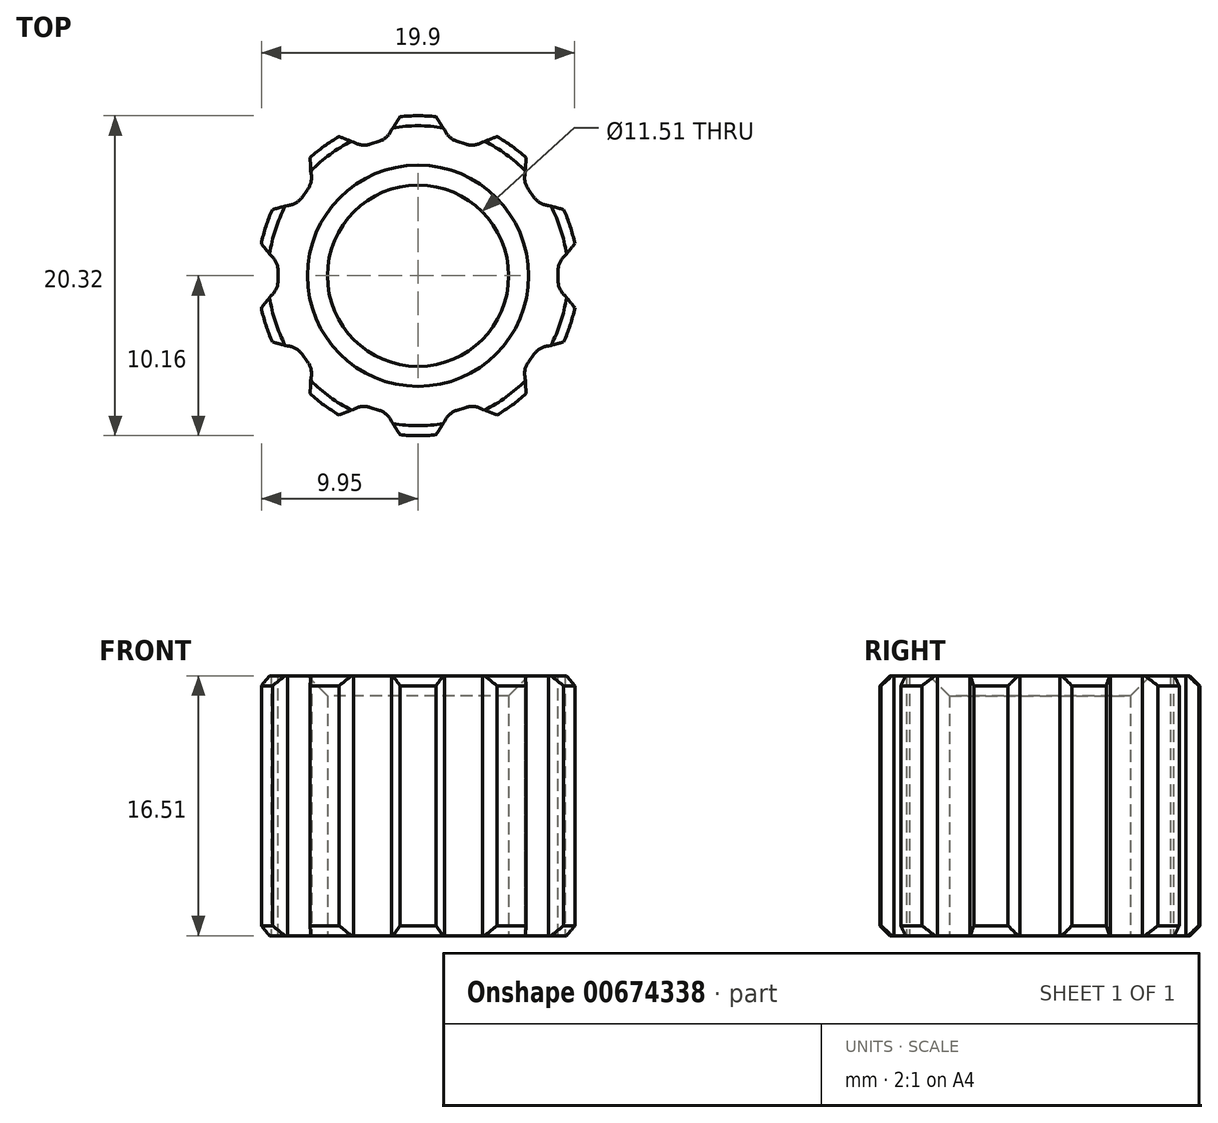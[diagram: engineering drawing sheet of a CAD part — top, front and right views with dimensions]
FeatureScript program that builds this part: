
annotation { "Feature Type Name" : "Feature", "Feature Type Description" : "" }
export const myFeature = defineFeature(function(context is Context, id is Id, definition is map)
    precondition{}
    {
        {
            var Q0;
            Q0=qCreatedBy(makeId("Top.planeOp"),FACE);
            var sketch = newSketch(context, id + "F0", { "sketchPlane" : qUnion([Q0])});
            skCircle(sketch, "E0", {"center": v(0, 0) * mm, "radius": 10.16 * mm});
            skCircle(sketch, "E1", {"center": v(0, 0) * mm, "radius": 5.75 * mm});
            skLineSegment(sketch, "E2.bottom", {"start": v(11.52, 1.27) * mm, "end": v(8.9, 1.27) * mm});
            skLineSegment(sketch, "E2.top", {"start": v(11.52, -1.27) * mm, "end": v(8.9, -1.27) * mm});
            skLineSegment(sketch, "E2.left", {"start": v(11.52, 1.27) * mm, "end": v(11.52, -1.27) * mm});
            skLineSegment(sketch, "E2.right", {"start": v(8.9, 1.27) * mm, "end": v(8.9, -1.27) * mm});
            skLineSegment(sketch, "E3.1.0", {"start": v(8.57, 7.8) * mm, "end": v(6.45, 6.25) * mm});
            skLineSegment(sketch, "E3.1.1", {"start": v(6.45, 6.25) * mm, "end": v(7.94, 4.2) * mm});
            skLineSegment(sketch, "E3.1.2", {"start": v(10.07, 5.74) * mm, "end": v(7.94, 4.2) * mm});
            skLineSegment(sketch, "E3.1.3", {"start": v(8.57, 7.8) * mm, "end": v(10.07, 5.74) * mm});
            skLineSegment(sketch, "E3.2.0", {"start": v(2.35, 11.35) * mm, "end": v(1.54, 8.85) * mm});
            skLineSegment(sketch, "E3.2.1", {"start": v(1.54, 8.85) * mm, "end": v(3.96, 8.06) * mm});
            skLineSegment(sketch, "E3.2.2", {"start": v(4.77, 10.57) * mm, "end": v(3.96, 8.06) * mm});
            skLineSegment(sketch, "E3.2.3", {"start": v(2.35, 11.35) * mm, "end": v(4.77, 10.57) * mm});
            skLineSegment(sketch, "E3.3.0", {"start": v(-4.77, 10.57) * mm, "end": v(-3.96, 8.06) * mm});
            skLineSegment(sketch, "E3.3.1", {"start": v(-3.96, 8.06) * mm, "end": v(-1.54, 8.85) * mm});
            skLineSegment(sketch, "E3.3.2", {"start": v(-2.35, 11.35) * mm, "end": v(-1.54, 8.85) * mm});
            skLineSegment(sketch, "E3.3.3", {"start": v(-4.77, 10.57) * mm, "end": v(-2.35, 11.35) * mm});
            skLineSegment(sketch, "E3.4.0", {"start": v(-10.07, 5.74) * mm, "end": v(-7.94, 4.2) * mm});
            skLineSegment(sketch, "E3.4.1", {"start": v(-7.94, 4.2) * mm, "end": v(-6.45, 6.25) * mm});
            skLineSegment(sketch, "E3.4.2", {"start": v(-8.57, 7.8) * mm, "end": v(-6.45, 6.25) * mm});
            skLineSegment(sketch, "E3.4.3", {"start": v(-10.07, 5.74) * mm, "end": v(-8.57, 7.8) * mm});
            skLineSegment(sketch, "E3.5.0", {"start": v(-11.52, -1.27) * mm, "end": v(-8.9, -1.27) * mm});
            skLineSegment(sketch, "E3.5.1", {"start": v(-8.9, -1.27) * mm, "end": v(-8.9, 1.27) * mm});
            skLineSegment(sketch, "E3.5.2", {"start": v(-11.52, 1.27) * mm, "end": v(-8.9, 1.27) * mm});
            skLineSegment(sketch, "E3.5.3", {"start": v(-11.52, -1.27) * mm, "end": v(-11.52, 1.27) * mm});
            skLineSegment(sketch, "E3.6.0", {"start": v(-8.57, -7.8) * mm, "end": v(-6.45, -6.25) * mm});
            skLineSegment(sketch, "E3.6.1", {"start": v(-6.45, -6.25) * mm, "end": v(-7.94, -4.2) * mm});
            skLineSegment(sketch, "E3.6.2", {"start": v(-10.07, -5.74) * mm, "end": v(-7.94, -4.2) * mm});
            skLineSegment(sketch, "E3.6.3", {"start": v(-8.57, -7.8) * mm, "end": v(-10.07, -5.74) * mm});
            skLineSegment(sketch, "E3.7.0", {"start": v(-2.35, -11.35) * mm, "end": v(-1.54, -8.85) * mm});
            skLineSegment(sketch, "E3.7.1", {"start": v(-1.54, -8.85) * mm, "end": v(-3.96, -8.06) * mm});
            skLineSegment(sketch, "E3.7.2", {"start": v(-4.77, -10.57) * mm, "end": v(-3.96, -8.06) * mm});
            skLineSegment(sketch, "E3.7.3", {"start": v(-2.35, -11.35) * mm, "end": v(-4.77, -10.57) * mm});
            skLineSegment(sketch, "E3.8.0", {"start": v(4.77, -10.57) * mm, "end": v(3.96, -8.06) * mm});
            skLineSegment(sketch, "E3.8.1", {"start": v(3.96, -8.06) * mm, "end": v(1.54, -8.85) * mm});
            skLineSegment(sketch, "E3.8.2", {"start": v(2.35, -11.35) * mm, "end": v(1.54, -8.85) * mm});
            skLineSegment(sketch, "E3.8.3", {"start": v(4.77, -10.57) * mm, "end": v(2.35, -11.35) * mm});
            skLineSegment(sketch, "E3.9.0", {"start": v(10.07, -5.74) * mm, "end": v(7.94, -4.2) * mm});
            skLineSegment(sketch, "E3.9.1", {"start": v(7.94, -4.2) * mm, "end": v(6.45, -6.25) * mm});
            skLineSegment(sketch, "E3.9.2", {"start": v(8.57, -7.8) * mm, "end": v(6.45, -6.25) * mm});
            skLineSegment(sketch, "E3.9.3", {"start": v(10.07, -5.74) * mm, "end": v(8.57, -7.8) * mm});
            skSolve(sketch);
        }
        {
            var Q0;
            Q0=makeQuery(id+"F0.imprint","IMPRINT",FACE,{"disambiguationData":[TD([[makeQuery(id+"F0.imprint","IMPRINT",EDGE,{"derivedFrom":sQuery(id+"F0.wireOp",EDGE,"E1")}),-1.0]])]});
            extrude(context, id + "F1", {"entities" : qUnion([Q0]), "depth" : 16.5 * mm, "offsetDistance" : 25.4 * mm});
        }
        {
            var Q0;
            Q0=makeQuery(id+"F1.opExtrude","SWEPT_EDGE",EDGE,{"disambiguationData":[OSD([sQuery(id+"F0.wireOp",EDGE,"E0"),sQuery(id+"F0.wireOp",EDGE,"E3.1.0")])]});
            var Q1;
            Q1=makeQuery(id+"F1.opExtrude","SWEPT_EDGE",EDGE,{"disambiguationData":[OSD([sQuery(id+"F0.wireOp",EDGE,"E0"),sQuery(id+"F0.wireOp",EDGE,"E3.2.2")])]});
            var Q2;
            {var subQ0=sQuery(id+"F0.wireOp",EDGE,"E0");Q2=makeQuery(id+"F1.opExtrude","SWEPT_FACE",FACE,{"disambiguationData":[OSD([subQ0]),TDD([makeQuery(id+"F0.imprint","IMPRINT",EDGE,{"disambiguationData":[TD([[makeQuery(id+"F0.imprint","INTERSECT",VERTEX,{"derivedFrom":[subQ0,sQuery(id+"F0.wireOp",EDGE,"E3.1.2")]}),1.0]])],"derivedFrom":subQ0})])]});}
            var Q3;
            {var subQ0=sQuery(id+"F0.wireOp",EDGE,"E0");Q3=makeQuery(id+"F1.opExtrude","SWEPT_FACE",FACE,{"disambiguationData":[OSD([subQ0]),TDD([makeQuery(id+"F0.imprint","IMPRINT",EDGE,{"disambiguationData":[TD([[makeQuery(id+"F0.imprint","INTERSECT",VERTEX,{"derivedFrom":[subQ0,sQuery(id+"F0.wireOp",EDGE,"E3.1.0")]}),-1.0]])],"derivedFrom":subQ0})])]});}
            var Q4;
            {var subQ0=sQuery(id+"F0.wireOp",EDGE,"E0");Q4=makeQuery(id+"F1.opExtrude","SWEPT_FACE",FACE,{"disambiguationData":[OSD([subQ0]),TDD([makeQuery(id+"F0.imprint","IMPRINT",EDGE,{"disambiguationData":[TD([[makeQuery(id+"F0.imprint","INTERSECT",VERTEX,{"derivedFrom":[subQ0,sQuery(id+"F0.wireOp",EDGE,"E3.2.0")]}),-1.0]])],"derivedFrom":subQ0})])]});}
            var Q5;
            {var subQ0=sQuery(id+"F0.wireOp",EDGE,"E0");Q5=makeQuery(id+"F1.opExtrude","SWEPT_FACE",FACE,{"disambiguationData":[OSD([subQ0]),TDD([makeQuery(id+"F0.imprint","IMPRINT",EDGE,{"disambiguationData":[TD([[makeQuery(id+"F0.imprint","INTERSECT",VERTEX,{"derivedFrom":[subQ0,sQuery(id+"F0.wireOp",EDGE,"E3.3.0")]}),-1.0]])],"derivedFrom":subQ0})])]});}
            var Q6;
            {var subQ0=sQuery(id+"F0.wireOp",EDGE,"E0");Q6=makeQuery(id+"F1.opExtrude","SWEPT_FACE",FACE,{"disambiguationData":[OSD([subQ0]),TDD([makeQuery(id+"F0.imprint","IMPRINT",EDGE,{"disambiguationData":[TD([[makeQuery(id+"F0.imprint","INTERSECT",VERTEX,{"derivedFrom":[subQ0,sQuery(id+"F0.wireOp",EDGE,"E3.4.0")]}),-1.0]])],"derivedFrom":subQ0})])]});}
            var Q7;
            {var subQ0=sQuery(id+"F0.wireOp",EDGE,"E0");Q7=makeQuery(id+"F1.opExtrude","SWEPT_FACE",FACE,{"disambiguationData":[OSD([subQ0]),TDD([makeQuery(id+"F0.imprint","IMPRINT",EDGE,{"disambiguationData":[TD([[makeQuery(id+"F0.imprint","INTERSECT",VERTEX,{"derivedFrom":[subQ0,sQuery(id+"F0.wireOp",EDGE,"E3.5.0")]}),-1.0]])],"derivedFrom":subQ0})])]});}
            var Q8;
            {var subQ0=sQuery(id+"F0.wireOp",EDGE,"E0");Q8=makeQuery(id+"F1.opExtrude","SWEPT_FACE",FACE,{"disambiguationData":[OSD([subQ0]),TDD([makeQuery(id+"F0.imprint","IMPRINT",EDGE,{"disambiguationData":[TD([[makeQuery(id+"F0.imprint","INTERSECT",VERTEX,{"derivedFrom":[subQ0,sQuery(id+"F0.wireOp",EDGE,"E3.6.0")]}),-1.0]])],"derivedFrom":subQ0})])]});}
            var Q9;
            {var subQ0=sQuery(id+"F0.wireOp",EDGE,"E0");Q9=makeQuery(id+"F1.opExtrude","SWEPT_FACE",FACE,{"disambiguationData":[OSD([subQ0]),TDD([makeQuery(id+"F0.imprint","IMPRINT",EDGE,{"disambiguationData":[TD([[makeQuery(id+"F0.imprint","INTERSECT",VERTEX,{"derivedFrom":[subQ0,sQuery(id+"F0.wireOp",EDGE,"E3.7.0")]}),-1.0]])],"derivedFrom":subQ0})])]});}
            var Q10;
            {var subQ0=sQuery(id+"F0.wireOp",EDGE,"E0");Q10=makeQuery(id+"F1.opExtrude","SWEPT_FACE",FACE,{"disambiguationData":[OSD([subQ0]),TDD([makeQuery(id+"F0.imprint","IMPRINT",EDGE,{"disambiguationData":[TD([[makeQuery(id+"F0.imprint","INTERSECT",VERTEX,{"derivedFrom":[subQ0,sQuery(id+"F0.wireOp",EDGE,"E3.8.0")]}),-1.0]])],"derivedFrom":subQ0})])]});}
            var Q11;
            {var subQ0=sQuery(id+"F0.wireOp",EDGE,"E0");Q11=makeQuery(id+"F1.opExtrude","SWEPT_FACE",FACE,{"disambiguationData":[OSD([subQ0]),TDD([makeQuery(id+"F0.imprint","IMPRINT",EDGE,{"disambiguationData":[TD([[makeQuery(id+"F0.imprint","INTERSECT",VERTEX,{"derivedFrom":[subQ0,sQuery(id+"F0.wireOp",EDGE,"E3.9.0")]}),-1.0]])],"derivedFrom":subQ0})])]});}
            chamfer(context, id + "F2", {"entities" : qUnion([Q0, Q1, Q2, Q3, Q4, Q5, Q6, Q7, Q8, Q9, Q10, Q11]), "width" : 0.64 * mm, "tangentPropagation" : true});
        }
        {
            var Q0;
            Q0=makeQuery(id+"F1.opExtrude","CAP_EDGE",EDGE,{"disambiguationData":[OSD([sQuery(id+"F0.wireOp",EDGE,"E1")])],"isStart":false});
            chamfer(context, id + "F3", {"entities" : qUnion([Q0]), "width" : 1.27 * mm, "tangentPropagation" : true});
        }
        {
            var Q0;
            Q0=makeQuery(id+"F1.opExtrude","SWEPT_EDGE",EDGE,{"disambiguationData":[OSD([sQuery(id+"F0.wireOp",EDGE,"E3.8.0"),sQuery(id+"F0.wireOp",EDGE,"E3.8.1")])]});
            var Q1;
            Q1=makeQuery(id+"F1.opExtrude","SWEPT_EDGE",EDGE,{"disambiguationData":[OSD([sQuery(id+"F0.wireOp",EDGE,"E3.8.1"),sQuery(id+"F0.wireOp",EDGE,"E3.8.2")])]});
            var Q2;
            Q2=makeQuery(id+"F1.opExtrude","SWEPT_EDGE",EDGE,{"disambiguationData":[OSD([sQuery(id+"F0.wireOp",EDGE,"E3.7.0"),sQuery(id+"F0.wireOp",EDGE,"E3.7.1")])]});
            var Q3;
            Q3=makeQuery(id+"F1.opExtrude","SWEPT_EDGE",EDGE,{"disambiguationData":[OSD([sQuery(id+"F0.wireOp",EDGE,"E3.7.1"),sQuery(id+"F0.wireOp",EDGE,"E3.7.2")])]});
            var Q4;
            Q4=makeQuery(id+"F1.opExtrude","SWEPT_EDGE",EDGE,{"disambiguationData":[OSD([sQuery(id+"F0.wireOp",EDGE,"E3.6.0"),sQuery(id+"F0.wireOp",EDGE,"E3.6.1")])]});
            var Q5;
            Q5=makeQuery(id+"F1.opExtrude","SWEPT_EDGE",EDGE,{"disambiguationData":[OSD([sQuery(id+"F0.wireOp",EDGE,"E3.5.0"),sQuery(id+"F0.wireOp",EDGE,"E3.5.1")])]});
            var Q6;
            Q6=makeQuery(id+"F1.opExtrude","SWEPT_EDGE",EDGE,{"disambiguationData":[OSD([sQuery(id+"F0.wireOp",EDGE,"E3.4.1"),sQuery(id+"F0.wireOp",EDGE,"E3.4.2")])]});
            var Q7;
            Q7=makeQuery(id+"F1.opExtrude","SWEPT_EDGE",EDGE,{"disambiguationData":[OSD([sQuery(id+"F0.wireOp",EDGE,"E3.5.1"),sQuery(id+"F0.wireOp",EDGE,"E3.5.2")])]});
            var Q8;
            Q8=makeQuery(id+"F1.opExtrude","SWEPT_EDGE",EDGE,{"disambiguationData":[OSD([sQuery(id+"F0.wireOp",EDGE,"E3.6.1"),sQuery(id+"F0.wireOp",EDGE,"E3.6.2")])]});
            var Q9;
            Q9=makeQuery(id+"F1.opExtrude","SWEPT_EDGE",EDGE,{"disambiguationData":[OSD([sQuery(id+"F0.wireOp",EDGE,"E3.4.0"),sQuery(id+"F0.wireOp",EDGE,"E3.4.1")])]});
            var Q10;
            Q10=makeQuery(id+"F1.opExtrude","SWEPT_EDGE",EDGE,{"disambiguationData":[OSD([sQuery(id+"F0.wireOp",EDGE,"E3.3.0"),sQuery(id+"F0.wireOp",EDGE,"E3.3.1")])]});
            var Q11;
            Q11=makeQuery(id+"F1.opExtrude","SWEPT_EDGE",EDGE,{"disambiguationData":[OSD([sQuery(id+"F0.wireOp",EDGE,"E3.2.0"),sQuery(id+"F0.wireOp",EDGE,"E3.2.1")])]});
            var Q12;
            Q12=makeQuery(id+"F1.opExtrude","SWEPT_EDGE",EDGE,{"disambiguationData":[OSD([sQuery(id+"F0.wireOp",EDGE,"E3.1.1"),sQuery(id+"F0.wireOp",EDGE,"E3.1.2")])]});
            var Q13;
            Q13=makeQuery(id+"F1.opExtrude","SWEPT_EDGE",EDGE,{"disambiguationData":[OSD([sQuery(id+"F0.wireOp",EDGE,"E3.3.1"),sQuery(id+"F0.wireOp",EDGE,"E3.3.2")])]});
            var Q14;
            Q14=makeQuery(id+"F1.opExtrude","SWEPT_EDGE",EDGE,{"disambiguationData":[OSD([sQuery(id+"F0.wireOp",EDGE,"E3.2.1"),sQuery(id+"F0.wireOp",EDGE,"E3.2.2")])]});
            var Q15;
            Q15=makeQuery(id+"F1.opExtrude","SWEPT_EDGE",EDGE,{"disambiguationData":[OSD([sQuery(id+"F0.wireOp",EDGE,"E3.1.0"),sQuery(id+"F0.wireOp",EDGE,"E3.1.1")])]});
            var Q16;
            Q16=makeQuery(id+"F1.opExtrude","SWEPT_EDGE",EDGE,{"disambiguationData":[OSD([sQuery(id+"F0.wireOp",EDGE,"E2.top"),sQuery(id+"F0.wireOp",EDGE,"E2.right")])]});
            var Q17;
            Q17=makeQuery(id+"F1.opExtrude","SWEPT_EDGE",EDGE,{"disambiguationData":[OSD([sQuery(id+"F0.wireOp",EDGE,"E2.bottom"),sQuery(id+"F0.wireOp",EDGE,"E2.right")])]});
            var Q18;
            Q18=makeQuery(id+"F1.opExtrude","SWEPT_EDGE",EDGE,{"disambiguationData":[OSD([sQuery(id+"F0.wireOp",EDGE,"E3.9.0"),sQuery(id+"F0.wireOp",EDGE,"E3.9.1")])]});
            var Q19;
            Q19=makeQuery(id+"F1.opExtrude","SWEPT_EDGE",EDGE,{"disambiguationData":[OSD([sQuery(id+"F0.wireOp",EDGE,"E3.9.1"),sQuery(id+"F0.wireOp",EDGE,"E3.9.2")])]});
            fillet(context, id + "F4", {"entities" : qUnion([Q0, Q1, Q2, Q3, Q4, Q5, Q6, Q7, Q8, Q9, Q10, Q11, Q12, Q13, Q14, Q15, Q16, Q17, Q18, Q19]), "radius" : 1.27 * mm, "tangentPropagation" : true, "allowEdgeOverflow" : false});
        }
    });
